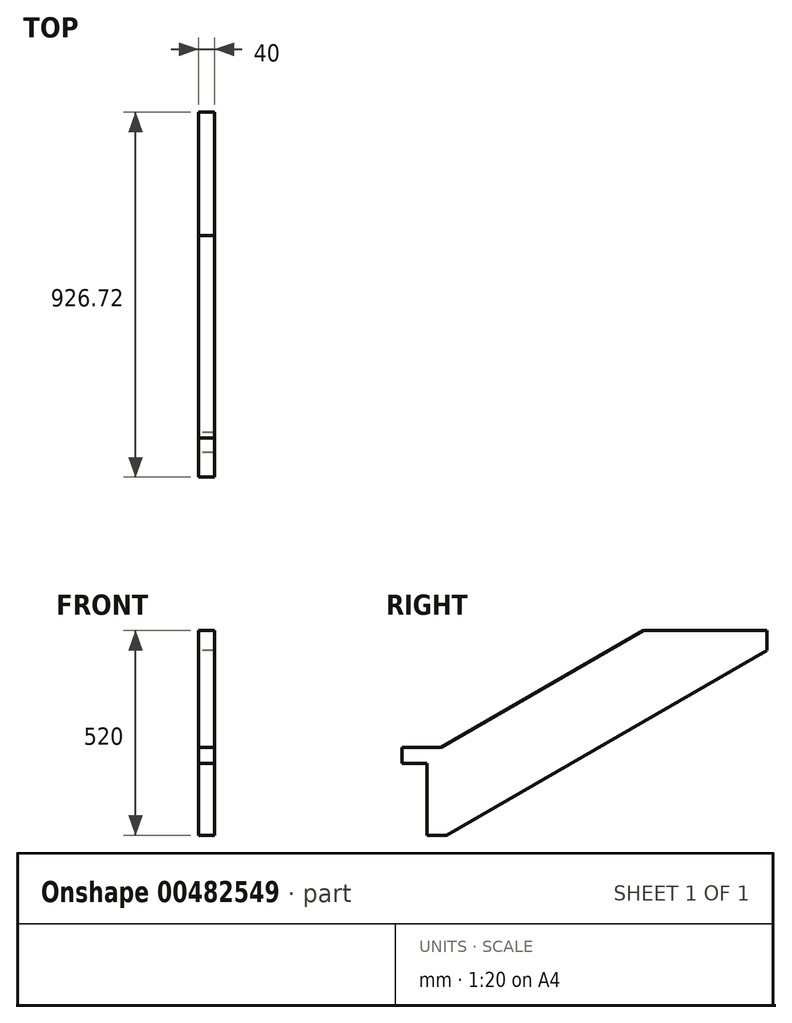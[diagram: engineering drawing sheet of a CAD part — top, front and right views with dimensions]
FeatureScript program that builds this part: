
annotation { "Feature Type Name" : "Feature", "Feature Type Description" : "" }
export const myFeature = defineFeature(function(context is Context, id is Id, definition is map)
    precondition{}
    {
        {
            var Q0;
            Q0=qCreatedBy(makeId("Right.planeOp"),FACE);
            var sketch = newSketch(context, id + "F0", { "sketchPlane" : qUnion([Q0])});
            skLineSegment(sketch, "E0", {"start": v(100, 202.07) * mm, "end": v(650.67, 520) * mm});
            skLineSegment(sketch, "E1", {"start": v(650.67, 520) * mm, "end": v(964.06, 520) * mm});
            skLineSegment(sketch, "E2", {"start": v(964.06, 520) * mm, "end": v(964.06, 470) * mm});
            skLineSegment(sketch, "E3", {"start": v(964.06, 470) * mm, "end": v(150, 0) * mm});
            skLineSegment(sketch, "E4", {"start": v(150, 0) * mm, "end": v(100, 0) * mm});
            skLineSegment(sketch, "E5", {"start": v(100, 0) * mm, "end": v(100, 202.07) * mm});
            skLineSegment(sketch, "E6.bottom", {"start": v(37.34, 182.93) * mm, "end": v(357.34, 182.93) * mm});
            skLineSegment(sketch, "E6.top", {"start": v(37.34, 222.93) * mm, "end": v(357.34, 222.93) * mm});
            skLineSegment(sketch, "E6.left", {"start": v(37.34, 182.93) * mm, "end": v(37.34, 222.93) * mm});
            skLineSegment(sketch, "E6.right", {"start": v(357.34, 182.93) * mm, "end": v(357.34, 222.93) * mm});
            skSolve(sketch);
        }
        {
            var Q0;
            Q0 = qSketchRegion(id + "F0", true);
            extrude(context, id + "F1", {"entities" : qUnion([Q0]), "depth" : 40 * mm});
        }
    });
